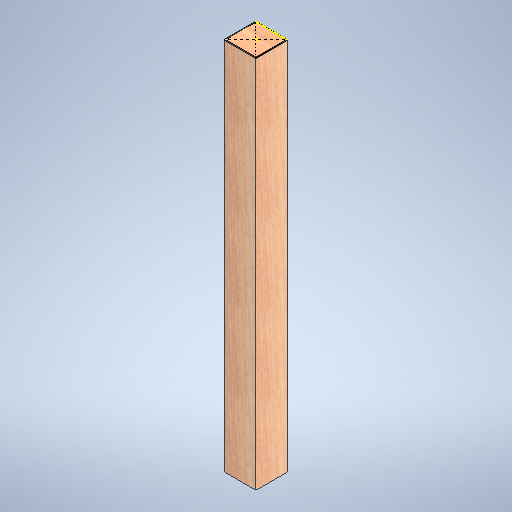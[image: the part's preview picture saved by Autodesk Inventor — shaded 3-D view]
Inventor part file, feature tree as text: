
AUTODESK INVENTOR PART (.ipt)
format: ipt  version: 2025 (Build 290162000, 162)  size: 331,264 bytes
history: native  units: in
note: dims shown in document units (in); Inventor stores cm internally (conversion verified against a paired STEP export)
features: sketch x2, extrude x1
ambient origin geometry x8: Origin, YZ Plane, XZ Plane, XY Plane, X Axis, Y Axis, Z Axis, Center Point
bodies: Solid1 (feature_tree)
feature tree (3):
  extrude  "Extrusion1"  Depth=4.0in
  sketch  "Sketch2"  dims[d2=48.0in d3=0.0in d4=0.5in d5=0.0344in d6=0.5in d7=0.0344in]
  sketch  "Sketch1"  dims[d0=4.0in d1=4.0in]
